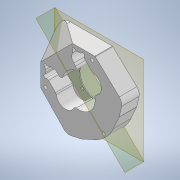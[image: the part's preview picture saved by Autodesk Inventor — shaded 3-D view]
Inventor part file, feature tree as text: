
AUTODESK INVENTOR PART (.ipt)
format: ipt  version: 2022 (Build 260153000, 153)  size: 264,192 bytes
history: native  units: in
note: dims shown in document units (in); Inventor stores cm internally (conversion verified against a paired STEP export)
features: extrude x3, sketch x3, other x3, plane x2, fillet x1, reference x1, projected_geometry x1
ambient origin geometry x8: Origin, YZ Plane, XZ Plane, XY Plane, X Axis, Y Axis, Z Axis, Center Point
bodies: Solid1 (feature_tree)
feature tree (14):
  plane  "Work Plane1"
  extrude  "Extrusion1"  Depth=1.0in
  extrude  "Extrusion2"  Depth=0.1679in
  fillet  "Fillet1"  Radius=0.7874in
  plane  "Work Plane2"
  extrude  "Extrusion3"  Depth=0.125in
  sketch  "Sketch1"  dims[d0=1.75in d1=1.0in]
  reference  "Reference1"
  sketch  "Sketch2"  dims[d2=45.0deg d3=0.1679in d4=0.7874in d6=360.0deg]
  projected_geometry  "Projected Loop1"
  sketch  "Sketch3"  dims[d8=0.0472in d9=0.0in d10=1.0in d11=1.0in d12=135.0deg d13=0.75in d14=1.0in d15=135.0deg d16=0.89in d17=0.0in d18=0.125in d19=45.0deg d20=0.0in d21=0.0in]
  other  "<userpath>\Documents\CAD\guardSwerve1\Assembly1.iam"
  other  "Assembly1.iam"
  other  "midblock"
